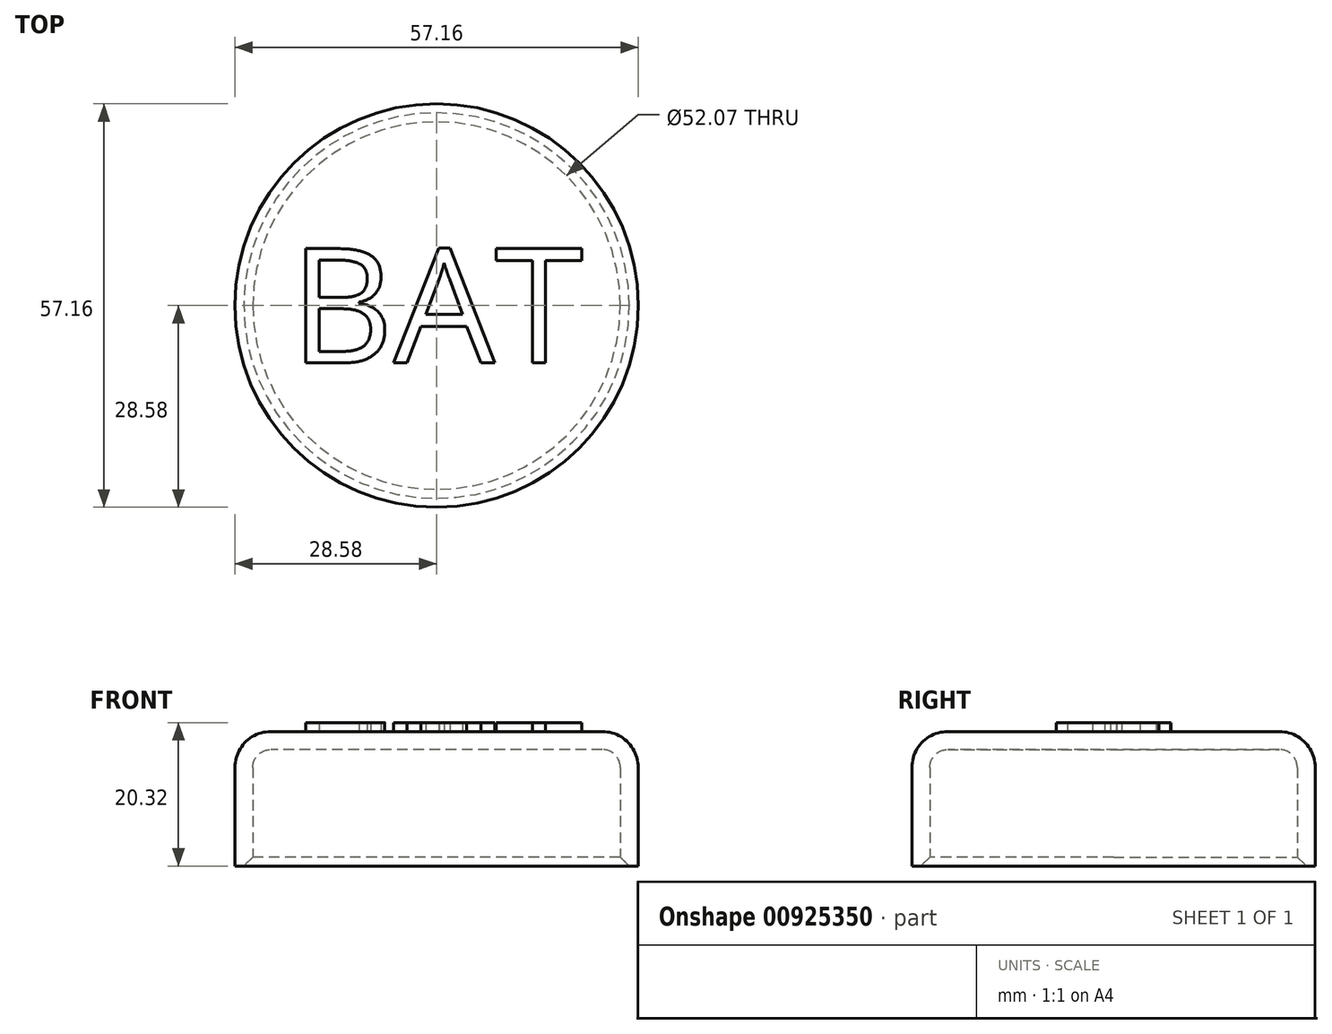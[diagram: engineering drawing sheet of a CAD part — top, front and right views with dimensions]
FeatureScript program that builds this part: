
annotation { "Feature Type Name" : "Feature", "Feature Type Description" : "" }
export const myFeature = defineFeature(function(context is Context, id is Id, definition is map)
    precondition{}
    {
        {
            var Q0;
            Q0=qCreatedBy(makeId("Top.planeOp"),FACE);
            var sketch = newSketch(context, id + "F0", { "sketchPlane" : qUnion([Q0])});
            skCircle(sketch, "E0", {"center": v(0, 0) * mm, "radius": 28.58 * mm});
            skSolve(sketch);
        }
        {
            var Q0;
            Q0=makeQuery(id+"F0.imprint","IMPRINT",FACE,{"disambiguationData":[TD([[makeQuery(id+"F0.imprint","IMPRINT",EDGE,{"derivedFrom":sQuery(id+"F0.wireOp",EDGE,"E0")}),1.0]])]});
            extrude(context, id + "F1", {"entities" : qUnion([Q0]), "depth" : 19.05 * mm, "offsetDistance" : 25.4 * mm});
        }
        {
            var Q0;
            Q0=makeQuery(id+"F1.opExtrude","CAP_EDGE",EDGE,{"disambiguationData":[OSD([sQuery(id+"F0.wireOp",EDGE,"E0")])],"isStart":false});
            fillet(context, id + "F2", {"entities" : qUnion([Q0]), "radius" : 5.08 * mm, "tangentPropagation" : true, "allowEdgeOverflow" : false});
        }
        {
            var Q0;
            Q0=makeQuery(id+"F1.opExtrude","CAP_FACE",FACE,{"disambiguationData":[OSD([sQuery(id+"F0.wireOp",EDGE,"E0")])],"isStart":true});
            shell(context, id + "F3", {"entities" : qUnion([Q0]), "thickness" : 2.54 * mm});
        }
        {
            var Q0;
            Q0=makeQuery(id+"F1.opExtrude","CAP_FACE",FACE,{"disambiguationData":[OSD([sQuery(id+"F0.wireOp",EDGE,"E0")])],"isStart":false});
            var sketch = newSketch(context, id + "F4", { "sketchPlane" : qUnion([Q0])});
            skText(sketch, "E1", { "text": "BAT", "fontName": "OpenSans-Regular.ttf"});
            const initialGuessF4  = {"E1": [-0.02075, -0.0081, 1, 0, 0.0163]};
            skSetInitialGuess(sketch, initialGuessF4);
            skSolve(sketch);
        }
        {
            var Q0;
            Q0 = qSketchRegion(id + "F4", true);
            extrude(context, id + "F5", {"entities" : qUnion([Q0]), "operationType" : NewBodyOperationType.ADD, "depth" : 1.27 * mm, "offsetDistance" : 25.4 * mm});
        }
        {
            var Q0;
            {var subQ0=sQuery(id+"F0.wireOp",EDGE,"E0");Q0=makeQuery(id+"F3.opShell","OFFSET_EDGE",EDGE,{"disambiguationData":[OSD([subQ0]),TDD([makeQuery(id+"F1.opExtrude","CAP_EDGE",EDGE,{"disambiguationData":[OSD([subQ0])],"isStart":true})])]});}
            chamfer(context, id + "F6", {"entities" : qUnion([Q0]), "width" : 1.27 * mm, "tangentPropagation" : true});
        }
    });
